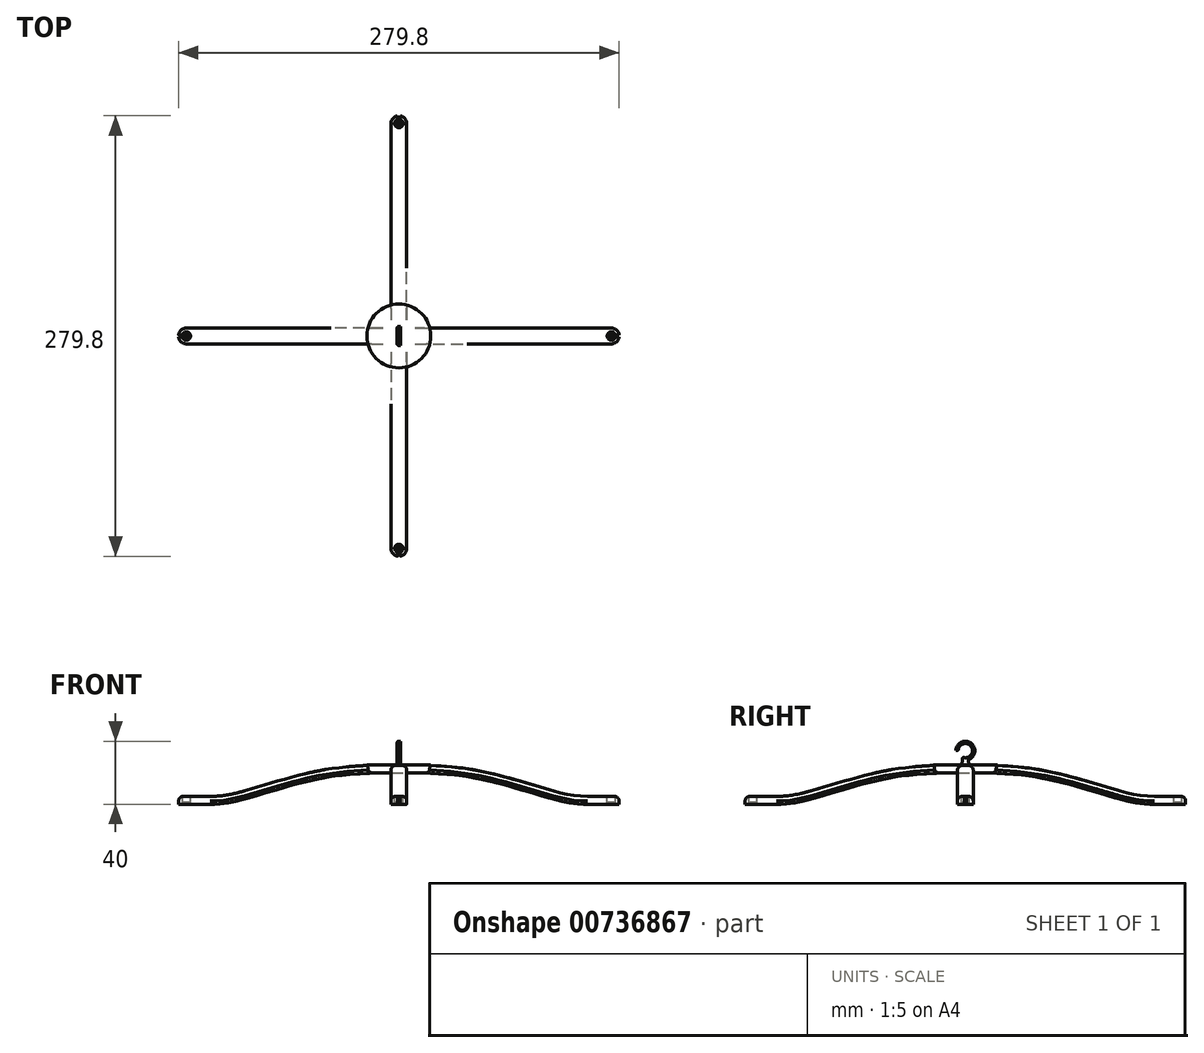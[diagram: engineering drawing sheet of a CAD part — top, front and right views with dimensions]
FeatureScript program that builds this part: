
annotation { "Feature Type Name" : "Feature", "Feature Type Description" : "" }
export const myFeature = defineFeature(function(context is Context, id is Id, definition is map)
    precondition{}
    {
        {
            var Q0;
            Q0=qCreatedBy(makeId("Front.planeOp"),FACE);
            var sketch = newSketch(context, id + "F0", { "sketchPlane" : qUnion([Q0])});
            skLineSegment(sketch, "E0", {"start": v(-62.22, 0) * mm, "end": v(-42.18, 0) * mm});
            skLineSegment(sketch, "E1", {"start": v(-62.22, 0) * mm, "end": v(-62.22, 5) * mm});
            skLineSegment(sketch, "E2", {"start": v(-62.22, 5) * mm, "end": v(-42.22, 5) * mm});
            skLineSegment(sketch, "E3", {"start": v(77.74, 5) * mm, "end": v(77.74, 25) * mm, "construction": true});
            skLineSegment(sketch, "E4", {"start": v(77.74, 25) * mm, "end": v(67.77, 25) * mm});
            skFitSpline(sketch, "E5", {"points": [v(67.77, 25) * mm, v(23.32, 20.5) * mm, v(-27.8, 6.57) * mm, v(-42.22, 5) * mm], "startDerivative": vector(-111.46, -4) * mm, "endDerivative": vector(-56.25, 0) * mm});
            skFitSpline(sketch, "E6.0", {"points": [v(67.95, 20) * mm, v(63.3, 19.84) * mm, v(56.4, 19.59) * mm, v(47.01, 18.94) * mm, v(39.8, 18.2) * mm, v(33.6, 17.34) * mm, v(28.46, 16.44) * mm, v(24.52, 15.65) * mm, v(20.47, 14.75) * mm, v(14.94, 13.4) * mm, v(7.87, 11.49) * mm, v(-0.58, 9.04) * mm, v(-8.76, 6.6) * mm, v(-16.42, 4.35) * mm, v(-22.18, 2.76) * mm, v(-25.81, 1.88) * mm, v(-27.77, 1.45) * mm, v(-29.62, 1.08) * mm, v(-31.8, 0.7) * mm, v(-34.98, 0.28) * mm, v(-38.52, 0.02) * mm, v(-41.01, 0) * mm, v(-42.22, 0) * mm]});
            skLineSegment(sketch, "E7", {"start": v(67.86, 20) * mm, "end": v(77.74, 20) * mm});
            skLineSegment(sketch, "E8.MirrorCS", {"start": v(77.74, 25) * mm, "end": v(87.7, 25) * mm});
            skLineSegment(sketch, "E9.MirrorCS", {"start": v(87.62, 20) * mm, "end": v(77.74, 20) * mm});
            skFitSpline(sketch, "E10.MirrorCS", {"points": [v(87.7, 25) * mm, v(132.16, 20.5) * mm, v(183.29, 6.57) * mm, v(197.7, 5) * mm], "startDerivative": vector(111.46, -4) * mm, "endDerivative": vector(56.25, 0) * mm});
            skLineSegment(sketch, "E11.MirrorCS", {"start": v(217.7, 5) * mm, "end": v(197.7, 5) * mm});
            skLineSegment(sketch, "E12.MirrorCS", {"start": v(217.7, 0) * mm, "end": v(217.7, 5) * mm});
            skLineSegment(sketch, "E13.MirrorCS", {"start": v(217.7, 0) * mm, "end": v(197.7, 0) * mm});
            skFitSpline(sketch, "E14.0", {"points": [v(87.53, 20) * mm, v(92.17, 19.84) * mm, v(99.08, 19.59) * mm, v(108.47, 18.94) * mm, v(115.68, 18.2) * mm, v(121.89, 17.34) * mm, v(127.02, 16.44) * mm, v(130.96, 15.65) * mm, v(135, 14.75) * mm, v(140.54, 13.4) * mm, v(147.6, 11.49) * mm, v(156.07, 9.04) * mm, v(164.24, 6.6) * mm, v(171.9, 4.35) * mm, v(177.67, 2.76) * mm, v(181.3, 1.88) * mm, v(183.25, 1.45) * mm, v(185.1, 1.08) * mm, v(187.27, 0.7) * mm, v(190.46, 0.28) * mm, v(194, 0.02) * mm, v(196.5, 0) * mm, v(197.7, 0) * mm]});
            skPoint(sketch, "E15.orphan", {"position": v(-42.22, 0) * mm});
            skSolve(sketch);
        }
        {
            var Q0;
            Q0=makeQuery(id+"F0.imprint","IMPRINT",FACE,{"disambiguationData":[TD([[makeQuery(id+"F0.imprint","IMPRINT",EDGE,{"derivedFrom":sQuery(id+"F0.wireOp",EDGE,"E0")}),1.0]])]});
            extrude(context, id + "F1", {"entities" : qUnion([Q0]), "depth" : 10 * mm, "offsetDistance" : 25 * mm});
        }
        {
            var Q0;
            Q0=makeQuery(id+"F1.opExtrude","SWEPT_FACE",FACE,{"disambiguationData":[OSD([sQuery(id+"F0.wireOp",EDGE,"E4"),sQuery(id+"F0.wireOp",EDGE,"E8.MirrorCS")])]});
            var sketch = newSketch(context, id + "F2", { "sketchPlane" : qUnion([Q0])});
            skLineSegment(sketch, "E16", {"start": v(77.74, 0) * mm, "end": v(77.74, -10) * mm, "construction": true});
            skLineSegment(sketch, "E17", {"start": v(67.77, -5) * mm, "end": v(87.7, -5) * mm, "construction": true});
            skPoint(sketch, "E18", {"position": v(77.74, -5) * mm});
            skCircle(sketch, "E19", {"center": v(77.74, -5) * mm, "radius": 2.93 * mm, "construction": true});
            skSolve(sketch);
        }
        {
            var Q0;
            Q0=makeQuery(id+"F1.opExtrude","SWEPT_BODY",BODY,{"disambiguationData":[OSD([sQuery(id+"F0.wireOp",EDGE,"E0"),sQuery(id+"F0.wireOp",EDGE,"E1"),sQuery(id+"F0.wireOp",EDGE,"E2"),sQuery(id+"F0.wireOp",EDGE,"E4"),sQuery(id+"F0.wireOp",EDGE,"E5"),sQuery(id+"F0.wireOp",EDGE,"E6.0"),sQuery(id+"F0.wireOp",EDGE,"E7"),sQuery(id+"F0.wireOp",EDGE,"E8.MirrorCS"),sQuery(id+"F0.wireOp",EDGE,"E9.MirrorCS"),sQuery(id+"F0.wireOp",EDGE,"E10.MirrorCS"),sQuery(id+"F0.wireOp",EDGE,"E11.MirrorCS"),sQuery(id+"F0.wireOp",EDGE,"E12.MirrorCS"),sQuery(id+"F0.wireOp",EDGE,"E13.MirrorCS"),sQuery(id+"F0.wireOp",EDGE,"E14.0")])]});
            var Q1;
            Q1=qCreatedBy(makeId("Front.planeOp"),FACE);
            mirror(context, id + "F3", {"entities" : qUnion([Q0]), "mirrorPlane" : qUnion([Q1])});
        }
        {
            var Q0;
            Q0=makeQuery(id+"F3.opPattern","COPY",FACE,{"derivedFrom":makeQuery(id+"F1.opExtrude","SWEPT_FACE",FACE,{"disambiguationData":[OSD([sQuery(id+"F0.wireOp",EDGE,"E4"),sQuery(id+"F0.wireOp",EDGE,"E8.MirrorCS")])]}),"instanceName":"1"});
            var sketch = newSketch(context, id + "F4", { "sketchPlane" : qUnion([Q0])});
            skLineSegment(sketch, "E20", {"start": v(77.74, 10) * mm, "end": v(77.74, 0) * mm, "construction": true});
            skLineSegment(sketch, "E21", {"start": v(67.77, 5) * mm, "end": v(87.7, 5) * mm, "construction": true});
            skCircle(sketch, "E22", {"center": v(77.74, 5) * mm, "radius": 2.5 * mm, "construction": true});
            skSolve(sketch);
        }
        {
            var Q0;
            Q0=makeQuery(id+"F3.opPattern","COPY",BODY,{"derivedFrom":makeQuery(id+"F1.opExtrude","SWEPT_BODY",BODY,{"disambiguationData":[OSD([sQuery(id+"F0.wireOp",EDGE,"E0"),sQuery(id+"F0.wireOp",EDGE,"E1"),sQuery(id+"F0.wireOp",EDGE,"E2"),sQuery(id+"F0.wireOp",EDGE,"E4"),sQuery(id+"F0.wireOp",EDGE,"E5"),sQuery(id+"F0.wireOp",EDGE,"E6.0"),sQuery(id+"F0.wireOp",EDGE,"E7"),sQuery(id+"F0.wireOp",EDGE,"E8.MirrorCS"),sQuery(id+"F0.wireOp",EDGE,"E9.MirrorCS"),sQuery(id+"F0.wireOp",EDGE,"E10.MirrorCS"),sQuery(id+"F0.wireOp",EDGE,"E11.MirrorCS"),sQuery(id+"F0.wireOp",EDGE,"E12.MirrorCS"),sQuery(id+"F0.wireOp",EDGE,"E13.MirrorCS"),sQuery(id+"F0.wireOp",EDGE,"E14.0")])]}),"instanceName":"1"});
            var Q1;
            Q1=sQuery(id+"F4.wireOp",EDGE,"E22");
            transform(context, id + "F5", {"entities" : qUnion([Q0]), "transformType" : TransformType.ROTATION, "transformAxis" : qUnion([Q1]), "angle" : 90 * degree, "makeCopy" : false});
        }
        {
            var Q0;
            Q0=sQuery(id+"F4.wireOp",EDGE,"E21");
            cPoint(context, id + "F6", {"entities" : qUnion([Q0]), "parameter" : 0.5});
        }
        {
            var Q0;
            Q0=sQuery(id+"F2.wireOp",EDGE,"E16");
            cPoint(context, id + "F7", {"entities" : qUnion([Q0]), "parameter" : 0.5});
        }
        {
            var Q0;
            Q0=makeQuery(id+"F3.opPattern","COPY",BODY,{"derivedFrom":makeQuery(id+"F1.opExtrude","SWEPT_BODY",BODY,{"disambiguationData":[OSD([sQuery(id+"F0.wireOp",EDGE,"E0"),sQuery(id+"F0.wireOp",EDGE,"E1"),sQuery(id+"F0.wireOp",EDGE,"E2"),sQuery(id+"F0.wireOp",EDGE,"E4"),sQuery(id+"F0.wireOp",EDGE,"E5"),sQuery(id+"F0.wireOp",EDGE,"E6.0"),sQuery(id+"F0.wireOp",EDGE,"E7"),sQuery(id+"F0.wireOp",EDGE,"E8.MirrorCS"),sQuery(id+"F0.wireOp",EDGE,"E9.MirrorCS"),sQuery(id+"F0.wireOp",EDGE,"E10.MirrorCS"),sQuery(id+"F0.wireOp",EDGE,"E11.MirrorCS"),sQuery(id+"F0.wireOp",EDGE,"E12.MirrorCS"),sQuery(id+"F0.wireOp",EDGE,"E13.MirrorCS"),sQuery(id+"F0.wireOp",EDGE,"E14.0")])]}),"instanceName":"1"});
            var Q1;
            Q1 = qCreatedBy(id + "F6" ,VERTEX);
            var Q2;
            Q2 = qCreatedBy(id + "F7" ,VERTEX);
            transform(context, id + "F8", {"entities" : qUnion([Q0]), "transformType" : TransformType.TRANSLATION_ENTITY, "oppositeDirectionEntity" : false, "transformLine" : qUnion([Q1, Q2]), "makeCopy" : false});
        }
        {
            var Q0;
            Q0=makeQuery(id+"F1.opExtrude","SWEPT_BODY",BODY,{"disambiguationData":[OSD([sQuery(id+"F0.wireOp",EDGE,"E0"),sQuery(id+"F0.wireOp",EDGE,"E1"),sQuery(id+"F0.wireOp",EDGE,"E2"),sQuery(id+"F0.wireOp",EDGE,"E4"),sQuery(id+"F0.wireOp",EDGE,"E5"),sQuery(id+"F0.wireOp",EDGE,"E6.0"),sQuery(id+"F0.wireOp",EDGE,"E7"),sQuery(id+"F0.wireOp",EDGE,"E8.MirrorCS"),sQuery(id+"F0.wireOp",EDGE,"E9.MirrorCS"),sQuery(id+"F0.wireOp",EDGE,"E10.MirrorCS"),sQuery(id+"F0.wireOp",EDGE,"E11.MirrorCS"),sQuery(id+"F0.wireOp",EDGE,"E12.MirrorCS"),sQuery(id+"F0.wireOp",EDGE,"E13.MirrorCS"),sQuery(id+"F0.wireOp",EDGE,"E14.0")])]});
            var Q1;
            Q1=makeQuery(id+"F3.opPattern","COPY",BODY,{"derivedFrom":makeQuery(id+"F1.opExtrude","SWEPT_BODY",BODY,{"disambiguationData":[OSD([sQuery(id+"F0.wireOp",EDGE,"E0"),sQuery(id+"F0.wireOp",EDGE,"E1"),sQuery(id+"F0.wireOp",EDGE,"E2"),sQuery(id+"F0.wireOp",EDGE,"E4"),sQuery(id+"F0.wireOp",EDGE,"E5"),sQuery(id+"F0.wireOp",EDGE,"E6.0"),sQuery(id+"F0.wireOp",EDGE,"E7"),sQuery(id+"F0.wireOp",EDGE,"E8.MirrorCS"),sQuery(id+"F0.wireOp",EDGE,"E9.MirrorCS"),sQuery(id+"F0.wireOp",EDGE,"E10.MirrorCS"),sQuery(id+"F0.wireOp",EDGE,"E11.MirrorCS"),sQuery(id+"F0.wireOp",EDGE,"E12.MirrorCS"),sQuery(id+"F0.wireOp",EDGE,"E13.MirrorCS"),sQuery(id+"F0.wireOp",EDGE,"E14.0")])]}),"instanceName":"1"});
            booleanBodies(context, id + "F9", {"operationType" : BooleanOperationType.UNION, "tools" : qUnion([Q0, Q1])});
        }
        {
            var Q0;
            {var subQ0=makeQuery(id+"F1.opExtrude","SWEPT_FACE",FACE,{"disambiguationData":[OSD([sQuery(id+"F0.wireOp",EDGE,"E7"),sQuery(id+"F0.wireOp",EDGE,"E9.MirrorCS")])]});Q0=makeQuery(id+"F9.opBoolean","MERGE",FACE,{"derivedFrom":[subQ0,makeQuery(id+"F3.opPattern","COPY",FACE,{"derivedFrom":subQ0,"instanceName":"1"})]});}
            var sketch = newSketch(context, id + "F10", { "sketchPlane" : qUnion([Q0])});
            skLineSegment(sketch, "E23", {"start": v(77.74, 14.88) * mm, "end": v(77.74, -4.88) * mm, "construction": true});
            skCircle(sketch, "E24", {"center": v(77.74, 5) * mm, "radius": 20 * mm});
            skSolve(sketch);
        }
        {
            var Q0;
            Q0 = qSketchRegion(id + "F10", true);
            var Q1;
            {var subQ0=makeQuery(id+"F1.opExtrude","SWEPT_FACE",FACE,{"disambiguationData":[OSD([sQuery(id+"F0.wireOp",EDGE,"E4"),sQuery(id+"F0.wireOp",EDGE,"E8.MirrorCS")])]});Q1=makeQuery(id+"F9.opBoolean","MERGE",FACE,{"derivedFrom":[subQ0,makeQuery(id+"F3.opPattern","COPY",FACE,{"derivedFrom":subQ0,"instanceName":"1"})]});}
            extrude(context, id + "F11", {"entities" : qUnion([Q0]), "operationType" : NewBodyOperationType.ADD, "endBound" : BoundingType.UP_TO_SURFACE, "oppositeDirection" : true, "depth" : 25 * mm, "endBoundEntityFace" : qUnion([Q1]), "offsetDistance" : 25 * mm, "hasDraft" : true, "draftAngle" : 3 * degree});
        }
        {
            var Q0;
            Q0=makeQuery(id+"F3.opPattern","COPY",EDGE,{"derivedFrom":makeQuery(id+"F1.opExtrude","CAP_EDGE",EDGE,{"disambiguationData":[OSD([sQuery(id+"F0.wireOp",EDGE,"E1")])],"isStart":false}),"instanceName":"1"});
            var Q1;
            Q1=makeQuery(id+"F3.opPattern","COPY",EDGE,{"derivedFrom":makeQuery(id+"F1.opExtrude","CAP_EDGE",EDGE,{"disambiguationData":[OSD([sQuery(id+"F0.wireOp",EDGE,"E1")])],"isStart":true}),"instanceName":"1"});
            var Q2;
            Q2=makeQuery(id+"F1.opExtrude","CAP_EDGE",EDGE,{"disambiguationData":[OSD([sQuery(id+"F0.wireOp",EDGE,"E12.MirrorCS")])],"isStart":false});
            var Q3;
            Q3=makeQuery(id+"F1.opExtrude","CAP_EDGE",EDGE,{"disambiguationData":[OSD([sQuery(id+"F0.wireOp",EDGE,"E12.MirrorCS")])],"isStart":true});
            var Q4;
            Q4=makeQuery(id+"F3.opPattern","COPY",EDGE,{"derivedFrom":makeQuery(id+"F1.opExtrude","CAP_EDGE",EDGE,{"disambiguationData":[OSD([sQuery(id+"F0.wireOp",EDGE,"E12.MirrorCS")])],"isStart":true}),"instanceName":"1"});
            var Q5;
            Q5=makeQuery(id+"F3.opPattern","COPY",EDGE,{"derivedFrom":makeQuery(id+"F1.opExtrude","CAP_EDGE",EDGE,{"disambiguationData":[OSD([sQuery(id+"F0.wireOp",EDGE,"E12.MirrorCS")])],"isStart":false}),"instanceName":"1"});
            var Q6;
            Q6=makeQuery(id+"F1.opExtrude","CAP_EDGE",EDGE,{"disambiguationData":[OSD([sQuery(id+"F0.wireOp",EDGE,"E1")])],"isStart":true});
            var Q7;
            Q7=makeQuery(id+"F1.opExtrude","CAP_EDGE",EDGE,{"disambiguationData":[OSD([sQuery(id+"F0.wireOp",EDGE,"E1")])],"isStart":false});
            fillet(context, id + "F12", {"entities" : qUnion([Q0, Q1, Q2, Q3, Q4, Q5, Q6, Q7]), "radius" : 5 * mm, "tangentPropagation" : true, "allowEdgeOverflow" : false});
        }
        {
            var Q0;
            Q0=makeQuery(id+"F1.opExtrude","SWEPT_FACE",FACE,{"disambiguationData":[OSD([sQuery(id+"F0.wireOp",EDGE,"E2")])]});
            var sketch = newSketch(context, id + "F13", { "sketchPlane" : qUnion([Q0])});
            skCircle(sketch, "E25", {"center": v(-57.22, -5) * mm, "radius": 2.65 * mm});
            skSolve(sketch);
        }
        {
            var Q0;
            Q0=makeQuery(id+"F13.imprint","IMPRINT",FACE,{"disambiguationData":[TD([[makeQuery(id+"F13.imprint","IMPRINT",EDGE,{"derivedFrom":sQuery(id+"F13.wireOp",EDGE,"E25")}),1.0]])]});
            extrude(context, id + "F14", {"entities" : qUnion([Q0]), "operationType" : NewBodyOperationType.REMOVE, "oppositeDirection" : true, "depth" : 4 * mm, "offsetDistance" : 25 * mm});
        }
        {
            var Q0;
            Q0=makeQuery(id+"F3.opPattern","COPY",FACE,{"derivedFrom":makeQuery(id+"F1.opExtrude","SWEPT_FACE",FACE,{"disambiguationData":[OSD([sQuery(id+"F0.wireOp",EDGE,"E2")])]}),"instanceName":"1"});
            var sketch = newSketch(context, id + "F15", { "sketchPlane" : qUnion([Q0])});
            skCircle(sketch, "E26", {"center": v(77.74, -139.96) * mm, "radius": 2.65 * mm});
            skSolve(sketch);
        }
        {
            var Q0;
            Q0=makeQuery(id+"F15.imprint","IMPRINT",FACE,{"disambiguationData":[TD([[makeQuery(id+"F15.imprint","IMPRINT",EDGE,{"derivedFrom":sQuery(id+"F15.wireOp",EDGE,"E26")}),1.0]])]});
            extrude(context, id + "F16", {"entities" : qUnion([Q0]), "operationType" : NewBodyOperationType.REMOVE, "oppositeDirection" : true, "depth" : 4 * mm, "offsetDistance" : 25 * mm});
        }
        {
            var Q0;
            Q0=makeQuery(id+"F1.opExtrude","SWEPT_FACE",FACE,{"disambiguationData":[OSD([sQuery(id+"F0.wireOp",EDGE,"E11.MirrorCS")])]});
            var sketch = newSketch(context, id + "F17", { "sketchPlane" : qUnion([Q0])});
            skCircle(sketch, "E27", {"center": v(212.7, -5) * mm, "radius": 2.65 * mm});
            skSolve(sketch);
        }
        {
            var Q0;
            Q0 = qSketchRegion(id + "F17", true);
            extrude(context, id + "F18", {"entities" : qUnion([Q0]), "operationType" : NewBodyOperationType.REMOVE, "oppositeDirection" : true, "depth" : 4 * mm, "offsetDistance" : 25 * mm});
        }
        {
            var Q0;
            Q0=makeQuery(id+"F3.opPattern","COPY",FACE,{"derivedFrom":makeQuery(id+"F1.opExtrude","SWEPT_FACE",FACE,{"disambiguationData":[OSD([sQuery(id+"F0.wireOp",EDGE,"E11.MirrorCS")])]}),"instanceName":"1"});
            var sketch = newSketch(context, id + "F19", { "sketchPlane" : qUnion([Q0])});
            skCircle(sketch, "E28", {"center": v(77.74, 129.96) * mm, "radius": 2.65 * mm});
            skSolve(sketch);
        }
        {
            var Q0;
            Q0 = qSketchRegion(id + "F19", true);
            extrude(context, id + "F20", {"entities" : qUnion([Q0]), "operationType" : NewBodyOperationType.REMOVE, "oppositeDirection" : true, "depth" : 4 * mm, "offsetDistance" : 25 * mm});
        }
        {
            var Q0;
            Q0=qCreatedBy(makeId("Top.planeOp"),FACE);
            var sketch = newSketch(context, id + "F21", { "sketchPlane" : qUnion([Q0])});
            skLineSegment(sketch, "E29.bottom", {"start": v(-63.37, -4.25) * mm, "end": v(-55.37, -4.25) * mm});
            skLineSegment(sketch, "E29.top", {"start": v(-63.37, -5.75) * mm, "end": v(-55.37, -5.75) * mm});
            skLineSegment(sketch, "E29.left", {"start": v(-63.37, -4.25) * mm, "end": v(-63.37, -5.75) * mm});
            skLineSegment(sketch, "E29.right", {"start": v(-55.37, -4.25) * mm, "end": v(-55.37, -5.75) * mm});
            skSolve(sketch);
        }
        {
            var Q0;
            Q0=makeQuery(id+"F21.imprint","IMPRINT",FACE,{"disambiguationData":[TD([[makeQuery(id+"F21.imprint","IMPRINT",EDGE,{"derivedFrom":sQuery(id+"F21.wireOp",EDGE,"E29.bottom")}),-1.0]])]});
            extrude(context, id + "F22", {"entities" : qUnion([Q0]), "operationType" : NewBodyOperationType.REMOVE, "depth" : 25 * mm, "offsetDistance" : 25 * mm});
        }
        {
            var Q0;
            Q0=makeQuery(id+"F1.opExtrude","SWEPT_FACE",FACE,{"disambiguationData":[OSD([sQuery(id+"F0.wireOp",EDGE,"E13.MirrorCS")])]});
            var sketch = newSketch(context, id + "F23", { "sketchPlane" : qUnion([Q0])});
            skLineSegment(sketch, "E30.bottom", {"start": v(218.7, 4.25) * mm, "end": v(210.7, 4.25) * mm});
            skLineSegment(sketch, "E30.top", {"start": v(218.7, 5.75) * mm, "end": v(210.7, 5.75) * mm});
            skLineSegment(sketch, "E30.left", {"start": v(218.7, 4.25) * mm, "end": v(218.7, 5.75) * mm});
            skLineSegment(sketch, "E30.right", {"start": v(210.7, 4.25) * mm, "end": v(210.7, 5.75) * mm});
            skSolve(sketch);
        }
        {
            var Q0;
            {var subQ0=sQuery(id+"F23.wireOp",EDGE,"E30.right");Q0=makeQuery(id+"F23.imprint","IMPRINT",FACE,{"disambiguationData":[TD([[makeQuery(id+"F23.imprint","IMPRINT",EDGE,{"derivedFrom":subQ0}),-1.0]])]});}
            extrude(context, id + "F24", {"entities" : qUnion([Q0]), "operationType" : NewBodyOperationType.REMOVE, "oppositeDirection" : true, "depth" : 25 * mm, "offsetDistance" : 25 * mm});
        }
        {
            var Q0;
            Q0=makeQuery(id+"F3.opPattern","COPY",FACE,{"derivedFrom":makeQuery(id+"F1.opExtrude","SWEPT_FACE",FACE,{"disambiguationData":[OSD([sQuery(id+"F0.wireOp",EDGE,"E13.MirrorCS")])]}),"instanceName":"1"});
            var sketch = newSketch(context, id + "F25", { "sketchPlane" : qUnion([Q0])});
            skLineSegment(sketch, "E31.bottom", {"start": v(77, 145.96) * mm, "end": v(78.5, 145.96) * mm});
            skLineSegment(sketch, "E31.top", {"start": v(77, 137.96) * mm, "end": v(78.5, 137.96) * mm});
            skLineSegment(sketch, "E31.left", {"start": v(77, 145.96) * mm, "end": v(77, 137.96) * mm});
            skLineSegment(sketch, "E31.right", {"start": v(78.5, 145.96) * mm, "end": v(78.5, 137.96) * mm});
            skLineSegment(sketch, "E32.bottom", {"start": v(78.5, -135.96) * mm, "end": v(77, -135.96) * mm});
            skLineSegment(sketch, "E32.top", {"start": v(78.5, -127.96) * mm, "end": v(77, -127.96) * mm});
            skLineSegment(sketch, "E32.left", {"start": v(78.5, -135.96) * mm, "end": v(78.5, -127.96) * mm});
            skLineSegment(sketch, "E32.right", {"start": v(77, -135.96) * mm, "end": v(77, -127.96) * mm});
            skSolve(sketch);
        }
        {
            var Q0;
            {var subQ0=sQuery(id+"F25.wireOp",EDGE,"E32.top");Q0=makeQuery(id+"F25.imprint","IMPRINT",FACE,{"disambiguationData":[TD([[makeQuery(id+"F25.imprint","IMPRINT",EDGE,{"derivedFrom":subQ0}),1.0]])]});}
            var Q1;
            Q1=makeQuery(id+"F25.imprint","IMPRINT",FACE,{"disambiguationData":[TD([[makeQuery(id+"F25.imprint","IMPRINT",EDGE,{"derivedFrom":sQuery(id+"F25.wireOp",EDGE,"E31.bottom")}),-1.0]])]});
            extrude(context, id + "F26", {"entities" : qUnion([Q0, Q1]), "operationType" : NewBodyOperationType.REMOVE, "oppositeDirection" : true, "depth" : 25 * mm, "offsetDistance" : 25 * mm});
        }
        {
            var Q0;
            Q0=makeQuery(id+"F3.opPattern","COPY",EDGE,{"derivedFrom":makeQuery(id+"F1.opExtrude","CAP_EDGE",EDGE,{"disambiguationData":[OSD([sQuery(id+"F0.wireOp",EDGE,"E5")])],"isStart":false}),"instanceName":"1"});
            var Q1;
            Q1=makeQuery(id+"F1.opExtrude","CAP_EDGE",EDGE,{"disambiguationData":[OSD([sQuery(id+"F0.wireOp",EDGE,"E5")])],"isStart":false});
            var Q2;
            Q2=makeQuery(id+"F1.opExtrude","CAP_EDGE",EDGE,{"disambiguationData":[OSD([sQuery(id+"F0.wireOp",EDGE,"E5")])],"isStart":true});
            var Q3;
            Q3=makeQuery(id+"F3.opPattern","COPY",EDGE,{"derivedFrom":makeQuery(id+"F1.opExtrude","CAP_EDGE",EDGE,{"disambiguationData":[OSD([sQuery(id+"F0.wireOp",EDGE,"E2")])],"isStart":true}),"instanceName":"1"});
            var Q4;
            Q4=makeQuery(id+"F1.opExtrude","CAP_EDGE",EDGE,{"disambiguationData":[OSD([sQuery(id+"F0.wireOp",EDGE,"E10.MirrorCS")])],"isStart":false});
            var Q5;
            Q5=makeQuery(id+"F1.opExtrude","CAP_EDGE",EDGE,{"disambiguationData":[OSD([sQuery(id+"F0.wireOp",EDGE,"E10.MirrorCS")])],"isStart":true});
            var Q6;
            Q6=makeQuery(id+"F3.opPattern","COPY",EDGE,{"derivedFrom":makeQuery(id+"F1.opExtrude","CAP_EDGE",EDGE,{"disambiguationData":[OSD([sQuery(id+"F0.wireOp",EDGE,"E10.MirrorCS")])],"isStart":true}),"instanceName":"1"});
            var Q7;
            Q7=makeQuery(id+"F3.opPattern","COPY",EDGE,{"derivedFrom":makeQuery(id+"F1.opExtrude","CAP_EDGE",EDGE,{"disambiguationData":[OSD([sQuery(id+"F0.wireOp",EDGE,"E10.MirrorCS")])],"isStart":false}),"instanceName":"1"});
            fillet(context, id + "F27", {"entities" : qUnion([Q0, Q1, Q2, Q3, Q4, Q5, Q6, Q7]), "radius" : 3 * mm, "tangentPropagation" : true, "allowEdgeOverflow" : false});
        }
        {
            var Q0;
            {var subQ0=makeQuery(id+"F1.opExtrude","SWEPT_FACE",FACE,{"disambiguationData":[OSD([sQuery(id+"F0.wireOp",EDGE,"E4"),sQuery(id+"F0.wireOp",EDGE,"E8.MirrorCS")])]});Q0=makeQuery(id+"F11.opExtrude","TWEAK_EDGE",EDGE,{"derivedFrom":[makeQuery(id+"F9.opBoolean","MERGE",FACE,{"derivedFrom":[subQ0,makeQuery(id+"F3.opPattern","COPY",FACE,{"derivedFrom":subQ0,"instanceName":"1"})]}),makeQuery(id+"F10.imprint","IMPRINT",EDGE,{"derivedFrom":sQuery(id+"F10.wireOp",EDGE,"E24")})]});}
            var Q1;
            {var subQ0=sQuery(id+"F0.wireOp",EDGE,"E9.MirrorCS");var subQ1=sQuery(id+"F0.wireOp",EDGE,"E7");var subQ2=makeQuery(id+"F1.opExtrude","SWEPT_FACE",FACE,{"disambiguationData":[OSD([subQ1,subQ0])]});var subQ3=sQuery(id+"F10.wireOp",EDGE,"E24");var subQ4=makeQuery(id+"F1.opExtrude","CAP_FACE",FACE,{"disambiguationData":[OSD([sQuery(id+"F0.wireOp",EDGE,"E0"),sQuery(id+"F0.wireOp",EDGE,"E1"),sQuery(id+"F0.wireOp",EDGE,"E2"),sQuery(id+"F0.wireOp",EDGE,"E4"),sQuery(id+"F0.wireOp",EDGE,"E5"),sQuery(id+"F0.wireOp",EDGE,"E6.0"),subQ1,sQuery(id+"F0.wireOp",EDGE,"E8.MirrorCS"),subQ0,sQuery(id+"F0.wireOp",EDGE,"E10.MirrorCS"),sQuery(id+"F0.wireOp",EDGE,"E11.MirrorCS"),sQuery(id+"F0.wireOp",EDGE,"E12.MirrorCS"),sQuery(id+"F0.wireOp",EDGE,"E13.MirrorCS"),sQuery(id+"F0.wireOp",EDGE,"E14.0")])],"isStart":false});Q1=makeQuery(id+"F11.boolean.opBoolean","SPLIT",EDGE,{"disambiguationData":[TD([subQ4,subQ2,makeQuery(id+"F3.opPattern","COPY",FACE,{"derivedFrom":subQ4,"instanceName":"1"}),makeQuery(id+"F3.opPattern","COPY",FACE,{"derivedFrom":subQ2,"instanceName":"1"}),makeQuery(id+"F11.opExtrude","SWEPT_FACE",FACE,{"disambiguationData":[OSD([subQ3])]}),makeQuery(id+"F11.opExtrude","CAP_FACE",FACE,{"disambiguationData":[OSD([subQ3])],"isStart":true})])],"derivedFrom":makeQuery(id+"F11.opExtrude","CAP_EDGE",EDGE,{"disambiguationData":[OSD([subQ3])],"isStart":true})});}
            var Q2;
            Q2=makeQuery(id+"F1.opExtrude","SWEPT_EDGE",EDGE,{"disambiguationData":[OSD([sQuery(id+"F0.wireOp",EDGE,"E6.0"),sQuery(id+"F0.wireOp",EDGE,"E7")])]});
            var Q3;
            Q3=makeQuery(id+"F1.opExtrude","SWEPT_EDGE",EDGE,{"disambiguationData":[OSD([sQuery(id+"F0.wireOp",EDGE,"E9.MirrorCS"),sQuery(id+"F0.wireOp",EDGE,"E14.0")])]});
            var Q4;
            Q4=makeQuery(id+"F3.opPattern","COPY",EDGE,{"derivedFrom":makeQuery(id+"F1.opExtrude","SWEPT_EDGE",EDGE,{"disambiguationData":[OSD([sQuery(id+"F0.wireOp",EDGE,"E9.MirrorCS"),sQuery(id+"F0.wireOp",EDGE,"E14.0")])]}),"instanceName":"1"});
            var Q5;
            Q5=makeQuery(id+"F3.opPattern","COPY",EDGE,{"derivedFrom":makeQuery(id+"F1.opExtrude","SWEPT_EDGE",EDGE,{"disambiguationData":[OSD([sQuery(id+"F0.wireOp",EDGE,"E6.0"),sQuery(id+"F0.wireOp",EDGE,"E7")])]}),"instanceName":"1"});
            var Q6;
            {var subQ0=sQuery(id+"F0.wireOp",EDGE,"E14.0");var subQ1=sQuery(id+"F0.wireOp",EDGE,"E13.MirrorCS");var subQ2=sQuery(id+"F0.wireOp",EDGE,"E12.MirrorCS");var subQ3=sQuery(id+"F0.wireOp",EDGE,"E11.MirrorCS");var subQ4=sQuery(id+"F0.wireOp",EDGE,"E10.MirrorCS");var subQ5=sQuery(id+"F0.wireOp",EDGE,"E9.MirrorCS");var subQ6=sQuery(id+"F0.wireOp",EDGE,"E8.MirrorCS");var subQ7=sQuery(id+"F0.wireOp",EDGE,"E7");var subQ8=sQuery(id+"F0.wireOp",EDGE,"E6.0");var subQ9=sQuery(id+"F0.wireOp",EDGE,"E5");var subQ10=sQuery(id+"F0.wireOp",EDGE,"E4");var subQ11=sQuery(id+"F0.wireOp",EDGE,"E2");var subQ12=sQuery(id+"F0.wireOp",EDGE,"E1");var subQ13=sQuery(id+"F0.wireOp",EDGE,"E0");var subQ14=makeQuery(id+"F1.opExtrude","SWEPT_FACE",FACE,{"disambiguationData":[OSD([subQ7,subQ5])]});var subQ15=sQuery(id+"F10.wireOp",EDGE,"E24");Q6=makeQuery(id+"F11.boolean.opBoolean","SPLIT",EDGE,{"disambiguationData":[TD([makeQuery(id+"F1.opExtrude","CAP_FACE",FACE,{"disambiguationData":[OSD([subQ13,subQ12,subQ11,subQ10,subQ9,subQ8,subQ7,subQ6,subQ5,subQ4,subQ3,subQ2,subQ1,subQ0])],"isStart":true}),subQ14,makeQuery(id+"F3.opPattern","COPY",FACE,{"derivedFrom":makeQuery(id+"F1.opExtrude","CAP_FACE",FACE,{"disambiguationData":[OSD([subQ13,subQ12,subQ11,subQ10,subQ9,subQ8,subQ7,subQ6,subQ5,subQ4,subQ3,subQ2,subQ1,subQ0])],"isStart":false}),"instanceName":"1"}),makeQuery(id+"F3.opPattern","COPY",FACE,{"derivedFrom":subQ14,"instanceName":"1"}),makeQuery(id+"F11.opExtrude","SWEPT_FACE",FACE,{"disambiguationData":[OSD([subQ15])]}),makeQuery(id+"F11.opExtrude","CAP_FACE",FACE,{"disambiguationData":[OSD([subQ15])],"isStart":true})])],"derivedFrom":makeQuery(id+"F11.opExtrude","CAP_EDGE",EDGE,{"disambiguationData":[OSD([subQ15])],"isStart":true})});}
            var Q7;
            {var subQ0=sQuery(id+"F0.wireOp",EDGE,"E9.MirrorCS");var subQ1=sQuery(id+"F0.wireOp",EDGE,"E7");var subQ2=makeQuery(id+"F1.opExtrude","CAP_FACE",FACE,{"disambiguationData":[OSD([sQuery(id+"F0.wireOp",EDGE,"E0"),sQuery(id+"F0.wireOp",EDGE,"E1"),sQuery(id+"F0.wireOp",EDGE,"E2"),sQuery(id+"F0.wireOp",EDGE,"E4"),sQuery(id+"F0.wireOp",EDGE,"E5"),sQuery(id+"F0.wireOp",EDGE,"E6.0"),subQ1,sQuery(id+"F0.wireOp",EDGE,"E8.MirrorCS"),subQ0,sQuery(id+"F0.wireOp",EDGE,"E10.MirrorCS"),sQuery(id+"F0.wireOp",EDGE,"E11.MirrorCS"),sQuery(id+"F0.wireOp",EDGE,"E12.MirrorCS"),sQuery(id+"F0.wireOp",EDGE,"E13.MirrorCS"),sQuery(id+"F0.wireOp",EDGE,"E14.0")])],"isStart":true});var subQ3=makeQuery(id+"F1.opExtrude","SWEPT_FACE",FACE,{"disambiguationData":[OSD([subQ1,subQ0])]});var subQ4=sQuery(id+"F10.wireOp",EDGE,"E24");Q7=makeQuery(id+"F11.boolean.opBoolean","SPLIT",EDGE,{"disambiguationData":[TD([subQ2,subQ3,makeQuery(id+"F3.opPattern","COPY",FACE,{"derivedFrom":subQ2,"instanceName":"1"}),makeQuery(id+"F3.opPattern","COPY",FACE,{"derivedFrom":subQ3,"instanceName":"1"}),makeQuery(id+"F11.opExtrude","SWEPT_FACE",FACE,{"disambiguationData":[OSD([subQ4])]}),makeQuery(id+"F11.opExtrude","CAP_FACE",FACE,{"disambiguationData":[OSD([subQ4])],"isStart":true})])],"derivedFrom":makeQuery(id+"F11.opExtrude","CAP_EDGE",EDGE,{"disambiguationData":[OSD([subQ4])],"isStart":true})});}
            var Q8;
            {var subQ0=sQuery(id+"F0.wireOp",EDGE,"E9.MirrorCS");var subQ1=sQuery(id+"F0.wireOp",EDGE,"E7");var subQ2=makeQuery(id+"F1.opExtrude","SWEPT_FACE",FACE,{"disambiguationData":[OSD([subQ1,subQ0])]});var subQ3=sQuery(id+"F10.wireOp",EDGE,"E24");var subQ4=sQuery(id+"F0.wireOp",EDGE,"E14.0");var subQ5=sQuery(id+"F0.wireOp",EDGE,"E13.MirrorCS");var subQ6=sQuery(id+"F0.wireOp",EDGE,"E12.MirrorCS");var subQ7=sQuery(id+"F0.wireOp",EDGE,"E11.MirrorCS");var subQ8=sQuery(id+"F0.wireOp",EDGE,"E10.MirrorCS");var subQ9=sQuery(id+"F0.wireOp",EDGE,"E8.MirrorCS");var subQ10=sQuery(id+"F0.wireOp",EDGE,"E6.0");var subQ11=sQuery(id+"F0.wireOp",EDGE,"E5");var subQ12=sQuery(id+"F0.wireOp",EDGE,"E4");var subQ13=sQuery(id+"F0.wireOp",EDGE,"E2");var subQ14=sQuery(id+"F0.wireOp",EDGE,"E1");var subQ15=sQuery(id+"F0.wireOp",EDGE,"E0");Q8=makeQuery(id+"F11.boolean.opBoolean","SPLIT",EDGE,{"disambiguationData":[TD([makeQuery(id+"F1.opExtrude","CAP_FACE",FACE,{"disambiguationData":[OSD([subQ15,subQ14,subQ13,subQ12,subQ11,subQ10,subQ1,subQ9,subQ0,subQ8,subQ7,subQ6,subQ5,subQ4])],"isStart":false}),subQ2,makeQuery(id+"F3.opPattern","COPY",FACE,{"derivedFrom":makeQuery(id+"F1.opExtrude","CAP_FACE",FACE,{"disambiguationData":[OSD([subQ15,subQ14,subQ13,subQ12,subQ11,subQ10,subQ1,subQ9,subQ0,subQ8,subQ7,subQ6,subQ5,subQ4])],"isStart":true}),"instanceName":"1"}),makeQuery(id+"F3.opPattern","COPY",FACE,{"derivedFrom":subQ2,"instanceName":"1"}),makeQuery(id+"F11.opExtrude","SWEPT_FACE",FACE,{"disambiguationData":[OSD([subQ3])]}),makeQuery(id+"F11.opExtrude","CAP_FACE",FACE,{"disambiguationData":[OSD([subQ3])],"isStart":true})])],"derivedFrom":makeQuery(id+"F11.opExtrude","CAP_EDGE",EDGE,{"disambiguationData":[OSD([subQ3])],"isStart":true})});}
            fillet(context, id + "F28", {"entities" : qUnion([Q0, Q1, Q2, Q3, Q4, Q5, Q6, Q7, Q8]), "radius" : 2 * mm, "tangentPropagation" : true, "allowEdgeOverflow" : false});
        }
        {
            var Q0;
            {var subQ0=sQuery(id+"F0.wireOp",EDGE,"E8.MirrorCS");var subQ1=sQuery(id+"F0.wireOp",EDGE,"E4");var subQ2=makeQuery(id+"F1.opExtrude","SWEPT_FACE",FACE,{"disambiguationData":[OSD([subQ1,subQ0])]});Q0=makeQuery(id+"F11.boolean.opBoolean","MERGE",FACE,{"derivedFrom":[makeQuery(id+"F9.opBoolean","MERGE",FACE,{"derivedFrom":[subQ2,makeQuery(id+"F3.opPattern","COPY",FACE,{"derivedFrom":subQ2,"instanceName":"1"})]}),makeQuery(id+"F11.opExtrude","CAP_FACE",FACE,{"disambiguationData":[OSD([subQ1,subQ0])],"isStart":false})]});}
            var sketch = newSketch(context, id + "F29", { "sketchPlane" : qUnion([Q0])});
            skLineSegment(sketch, "E33", {"start": v(79.63, 13.94) * mm, "end": v(75.85, -23.94) * mm, "construction": true});
            skLineSegment(sketch, "E34", {"start": v(58.8, -3.11) * mm, "end": v(96.68, -6.89) * mm, "construction": true});
            skLineSegment(sketch, "E35", {"start": v(77.74, -5) * mm, "end": v(77.74, 1) * mm, "construction": true});
            skLineSegment(sketch, "E36.bottom", {"start": v(78.74, 1) * mm, "end": v(76.74, 1) * mm});
            skLineSegment(sketch, "E36.top", {"start": v(78.74, -11) * mm, "end": v(76.74, -11) * mm});
            skLineSegment(sketch, "E36.left", {"start": v(78.74, 1) * mm, "end": v(78.74, -11) * mm});
            skLineSegment(sketch, "E36.right", {"start": v(76.74, 1) * mm, "end": v(76.74, -11) * mm});
            skSolve(sketch);
        }
        {
            var Q0;
            Q0=makeQuery(id+"F29.imprint","IMPRINT",FACE,{"disambiguationData":[TD([[makeQuery(id+"F29.imprint","IMPRINT",EDGE,{"derivedFrom":sQuery(id+"F29.wireOp",EDGE,"E36.bottom")}),1.0]])]});
            extrude(context, id + "F30", {"entities" : qUnion([Q0]), "operationType" : NewBodyOperationType.ADD, "depth" : 15 * mm, "offsetDistance" : 25 * mm});
        }
        {
            var Q0;
            Q0=makeQuery(id+"F30.opExtrude","SWEPT_FACE",FACE,{"disambiguationData":[OSD([sQuery(id+"F29.wireOp",EDGE,"E36.left")])]});
            var sketch = newSketch(context, id + "F31", { "sketchPlane" : qUnion([Q0])});
            skLineSegment(sketch, "E37", {"start": v(-5, 34) * mm, "end": v(-5, 25) * mm, "construction": true});
            skArc(sketch, "E38.0", {"start": v(-7, 29.97) * mm, "mid": v(-1.18, 36.37) * mm, "end": v(-9.5, 34) * mm});
            skLineSegment(sketch, "E39", {"start": v(-9.5, 34) * mm, "end": v(-11, 34) * mm});
            skLineSegment(sketch, "E40.bottom", {"start": v(-3, 25) * mm, "end": v(-7, 25) * mm});
            skLineSegment(sketch, "E40.left", {"start": v(-3, 25) * mm, "end": v(-3, 28.34) * mm});
            skLineSegment(sketch, "E40.right", {"start": v(-7, 25) * mm, "end": v(-7, 29.97) * mm});
            skArc(sketch, "E41.trimOffspring", {"start": v(-3, 28.34) * mm, "mid": v(-1.54, 38.9) * mm, "end": v(-11, 34) * mm});
            skPoint(sketch, "E42.orphan", {"position": v(-5, 40) * mm});
            skSolve(sketch);
        }
        {
            var Q0;
            {var subQ0=sQuery(id+"F31.wireOp",EDGE,"E41.trimOffspring");var subQ1=sQuery(id+"F29.wireOp",EDGE,"E36.left");var subQ4=makeQuery(id+"F30.opExtrude","CAP_EDGE",EDGE,{"disambiguationData":[OSD([subQ1])],"isStart":false});var subQ5=makeQuery(id+"F31.imprint","INTERSECT",VERTEX,{"derivedFrom":[subQ4,subQ0]});Q0=makeQuery(id+"F31.imprint","IMPRINT",FACE,{"disambiguationData":[TD([[makeQuery(id+"F31.imprint","IMPRINT",EDGE,{"disambiguationData":[TD([[subQ5,-1.0]])],"derivedFrom":subQ4}),1.0]])]});}
            var Q1;
            {var subQ0=sQuery(id+"F31.wireOp",EDGE,"E41.trimOffspring");var subQ1=sQuery(id+"F29.wireOp",EDGE,"E36.left");var subQ4=makeQuery(id+"F30.opExtrude","CAP_EDGE",EDGE,{"disambiguationData":[OSD([subQ1])],"isStart":false});var subQ5=makeQuery(id+"F31.imprint","INTERSECT",VERTEX,{"derivedFrom":[subQ4,subQ0]});Q1=makeQuery(id+"F31.imprint","IMPRINT",FACE,{"disambiguationData":[TD([[makeQuery(id+"F31.imprint","IMPRINT",EDGE,{"disambiguationData":[TD([[subQ5,1.0]])],"derivedFrom":subQ0}),-1.0]])]});}
            var Q2;
            Q2=makeQuery(id+"F31.imprint","IMPRINT",FACE,{"disambiguationData":[TD([[makeQuery(id+"F31.imprint","IMPRINT",EDGE,{"derivedFrom":sQuery(id+"F31.wireOp",EDGE,"E38.0")}),1.0]])]});
            var Q3;
            {var subQ0=sQuery(id+"F31.wireOp",EDGE,"E40.left");Q3=makeQuery(id+"F31.imprint","IMPRINT",FACE,{"disambiguationData":[TD([[makeQuery(id+"F31.imprint","IMPRINT",EDGE,{"derivedFrom":subQ0}),-1.0]])]});}
            extrude(context, id + "F32", {"entities" : qUnion([Q0, Q1, Q2, Q3]), "operationType" : NewBodyOperationType.REMOVE, "oppositeDirection" : true, "depth" : 25 * mm, "offsetDistance" : 25 * mm});
        }
        {
            var Q0;
            {var subQ0=sQuery(id+"F31.wireOp",EDGE,"E41.trimOffspring");var subQ1=sQuery(id+"F31.wireOp",EDGE,"E39");var subQ2=sQuery(id+"F29.wireOp",EDGE,"E36.left");var subQ3=sQuery(id+"F29.wireOp",EDGE,"E36.top");Q0=makeQuery(id+"F32.boolean.opBoolean","TWEAK_EDGE",EDGE,{"derivedFrom":[makeQuery(id+"F32.opExtrude","SWEPT_EDGE",EDGE,{"disambiguationData":[OSD([subQ3,subQ2,subQ1,subQ0]),OD(0.0)]}),makeQuery(id+"F32.opExtrude","SWEPT_EDGE",EDGE,{"disambiguationData":[OSD([subQ3,subQ2,subQ1,subQ0]),OD(1.0)]})]});}
            var Q1;
            Q1=makeQuery(id+"F32.boolean.opBoolean","COPY",EDGE,{"derivedFrom":makeQuery(id+"F32.opExtrude","CAP_EDGE",EDGE,{"disambiguationData":[OSD([sQuery(id+"F31.wireOp",EDGE,"E39")])],"isStart":true})});
            var Q2;
            {var subQ0=sQuery(id+"F31.wireOp",EDGE,"E41.trimOffspring");var subQ1=sQuery(id+"F29.wireOp",EDGE,"E36.left");var subQ2=makeQuery(id+"F31.imprint","INTERSECT",VERTEX,{"derivedFrom":[makeQuery(id+"F30.opExtrude","CAP_EDGE",EDGE,{"disambiguationData":[OSD([subQ1])],"isStart":false}),subQ0]});Q2=makeQuery(id+"F32.boolean.opBoolean","TWEAK_EDGE",EDGE,{"derivedFrom":[makeQuery(id+"F32.opExtrude","CAP_EDGE",EDGE,{"disambiguationData":[OSD([subQ0]),TDD([makeQuery(id+"F31.imprint","IMPRINT",EDGE,{"disambiguationData":[TD([[makeQuery(id+"F31.imprint","INTERSECT",VERTEX,{"derivedFrom":[sQuery(id+"F31.wireOp",EDGE,"E40.left"),subQ0]}),-1.0]])],"derivedFrom":subQ0})])],"isStart":true}),makeQuery(id+"F32.opExtrude","CAP_EDGE",EDGE,{"disambiguationData":[OSD([subQ0]),TDD([makeQuery(id+"F31.imprint","IMPRINT",EDGE,{"disambiguationData":[TD([[subQ2,1.0]])],"derivedFrom":subQ0})])],"isStart":true}),makeQuery(id+"F32.opExtrude","CAP_EDGE",EDGE,{"disambiguationData":[OSD([subQ0]),TDD([makeQuery(id+"F31.imprint","IMPRINT",EDGE,{"disambiguationData":[TD([[subQ2,-1.0]])],"derivedFrom":subQ0})])],"isStart":true})]});}
            var Q3;
            {var subQ0=sQuery(id+"F31.wireOp",EDGE,"E41.trimOffspring");var subQ1=sQuery(id+"F29.wireOp",EDGE,"E36.left");var subQ2=makeQuery(id+"F31.imprint","INTERSECT",VERTEX,{"derivedFrom":[makeQuery(id+"F30.opExtrude","CAP_EDGE",EDGE,{"disambiguationData":[OSD([subQ1])],"isStart":false}),subQ0]});Q3=makeQuery(id+"F32.boolean.opBoolean","INTERSECT",EDGE,{"derivedFrom":[makeQuery(id+"F30.opExtrude","SWEPT_FACE",FACE,{"disambiguationData":[OSD([sQuery(id+"F29.wireOp",EDGE,"E36.right")])]}),makeQuery(id+"F32.opExtrude","SWEPT_FACE",FACE,{"disambiguationData":[OSD([subQ0]),TDD([makeQuery(id+"F31.imprint","IMPRINT",EDGE,{"disambiguationData":[TD([[makeQuery(id+"F31.imprint","INTERSECT",VERTEX,{"derivedFrom":[sQuery(id+"F31.wireOp",EDGE,"E40.left"),subQ0]}),-1.0]])],"derivedFrom":subQ0})])]}),makeQuery(id+"F32.opExtrude","SWEPT_FACE",FACE,{"disambiguationData":[OSD([subQ0]),TDD([makeQuery(id+"F31.imprint","IMPRINT",EDGE,{"disambiguationData":[TD([[subQ2,1.0]])],"derivedFrom":subQ0})])]}),makeQuery(id+"F32.opExtrude","SWEPT_FACE",FACE,{"disambiguationData":[OSD([subQ0]),TDD([makeQuery(id+"F31.imprint","IMPRINT",EDGE,{"disambiguationData":[TD([[subQ2,-1.0]])],"derivedFrom":subQ0})])]})]});}
            var Q4;
            Q4=makeQuery(id+"F32.boolean.opBoolean","INTERSECT",EDGE,{"derivedFrom":[makeQuery(id+"F30.opExtrude","SWEPT_FACE",FACE,{"disambiguationData":[OSD([sQuery(id+"F29.wireOp",EDGE,"E36.right")])]}),makeQuery(id+"F32.opExtrude","SWEPT_FACE",FACE,{"disambiguationData":[OSD([sQuery(id+"F31.wireOp",EDGE,"E38.0")])]})]});
            var Q5;
            Q5=makeQuery(id+"F32.boolean.opBoolean","INTERSECT",EDGE,{"derivedFrom":[makeQuery(id+"F30.opExtrude","SWEPT_FACE",FACE,{"disambiguationData":[OSD([sQuery(id+"F29.wireOp",EDGE,"E36.right")])]}),makeQuery(id+"F32.opExtrude","SWEPT_FACE",FACE,{"disambiguationData":[OSD([sQuery(id+"F31.wireOp",EDGE,"E39")])]})]});
            var Q6;
            Q6=makeQuery(id+"F32.boolean.opBoolean","COPY",EDGE,{"derivedFrom":makeQuery(id+"F32.opExtrude","CAP_EDGE",EDGE,{"disambiguationData":[OSD([sQuery(id+"F31.wireOp",EDGE,"E38.0")])],"isStart":true})});
            var Q7;
            Q7=makeQuery(id+"F32.boolean.opBoolean","COPY",EDGE,{"derivedFrom":makeQuery(id+"F32.opExtrude","SWEPT_EDGE",EDGE,{"disambiguationData":[OSD([sQuery(id+"F31.wireOp",EDGE,"E38.0"),sQuery(id+"F31.wireOp",EDGE,"E40.right")])]})});
            var Q8;
            Q8=makeQuery(id+"F32.boolean.opBoolean","COPY",EDGE,{"derivedFrom":makeQuery(id+"F32.opExtrude","SWEPT_EDGE",EDGE,{"disambiguationData":[OSD([sQuery(id+"F31.wireOp",EDGE,"E38.0"),sQuery(id+"F31.wireOp",EDGE,"E39")])]})});
            fillet(context, id + "F33", {"entities" : qUnion([Q0, Q1, Q2, Q3, Q4, Q5, Q6, Q7, Q8]), "radius" : 0.75 * mm, "tangentPropagation" : true, "allowEdgeOverflow" : false});
        }
        {
            var Q0;
            Q0=makeQuery(id+"F30.opExtrude","CAP_EDGE",EDGE,{"disambiguationData":[OSD([sQuery(id+"F29.wireOp",EDGE,"E36.left")])],"isStart":true});
            var Q1;
            Q1=makeQuery(id+"F32.boolean.opBoolean","COPY",EDGE,{"derivedFrom":makeQuery(id+"F32.opExtrude","SWEPT_EDGE",EDGE,{"disambiguationData":[OSD([sQuery(id+"F29.wireOp",EDGE,"E36.left"),sQuery(id+"F31.wireOp",EDGE,"E40.bottom"),sQuery(id+"F31.wireOp",EDGE,"E40.right")])]})});
            var Q2;
            Q2=makeQuery(id+"F30.opExtrude","CAP_EDGE",EDGE,{"disambiguationData":[OSD([sQuery(id+"F29.wireOp",EDGE,"E36.right")])],"isStart":true});
            var Q3;
            Q3=makeQuery(id+"F32.boolean.opBoolean","COPY",EDGE,{"derivedFrom":makeQuery(id+"F32.opExtrude","SWEPT_EDGE",EDGE,{"disambiguationData":[OSD([sQuery(id+"F29.wireOp",EDGE,"E36.left"),sQuery(id+"F31.wireOp",EDGE,"E40.bottom"),sQuery(id+"F31.wireOp",EDGE,"E40.left")])]})});
            fillet(context, id + "F34", {"entities" : qUnion([Q0, Q1, Q2, Q3]), "radius" : 2 * mm, "tangentPropagation" : true, "allowEdgeOverflow" : false});
        }
        {
            var Q0;
            Q0=makeQuery(id+"F32.boolean.opBoolean","COPY",EDGE,{"derivedFrom":makeQuery(id+"F32.opExtrude","CAP_EDGE",EDGE,{"disambiguationData":[OSD([sQuery(id+"F31.wireOp",EDGE,"E40.left")])],"isStart":true})});
            var Q1;
            Q1=makeQuery(id+"F32.boolean.opBoolean","INTERSECT",EDGE,{"derivedFrom":[makeQuery(id+"F30.opExtrude","SWEPT_FACE",FACE,{"disambiguationData":[OSD([sQuery(id+"F29.wireOp",EDGE,"E36.right")])]}),makeQuery(id+"F32.opExtrude","SWEPT_FACE",FACE,{"disambiguationData":[OSD([sQuery(id+"F31.wireOp",EDGE,"E40.left")])]})]});
            var Q2;
            Q2=makeQuery(id+"F32.boolean.opBoolean","INTERSECT",EDGE,{"derivedFrom":[makeQuery(id+"F30.opExtrude","SWEPT_FACE",FACE,{"disambiguationData":[OSD([sQuery(id+"F29.wireOp",EDGE,"E36.right")])]}),makeQuery(id+"F32.opExtrude","SWEPT_FACE",FACE,{"disambiguationData":[OSD([sQuery(id+"F31.wireOp",EDGE,"E40.right")])]})]});
            var Q3;
            Q3=makeQuery(id+"F32.boolean.opBoolean","COPY",EDGE,{"derivedFrom":makeQuery(id+"F32.opExtrude","CAP_EDGE",EDGE,{"disambiguationData":[OSD([sQuery(id+"F31.wireOp",EDGE,"E40.right")])],"isStart":true})});
            fillet(context, id + "F35", {"entities" : qUnion([Q0, Q1, Q2, Q3]), "radius" : 1 * mm, "tangentPropagation" : true, "allowEdgeOverflow" : false});
        }
    });
